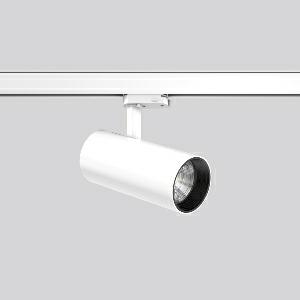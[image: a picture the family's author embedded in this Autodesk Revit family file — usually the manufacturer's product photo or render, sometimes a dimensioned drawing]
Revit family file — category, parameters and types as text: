
# Revit family: deecos_s_mini_742200_002_2_e126
name_source: partatom
category: Lighting Fixtures
units: mm (PartAtom-declared; Revit-internal decimal feet)

## family parameters
Cut with Voids When Loaded = No
Host = Face
Light Source = No
Part Type = Normal
Room Calculation Point = No
Round Connector Dimension = Use Diameter
Shared = No

## types (1)
- DEECOS S mini (1 x LED Modul 927, 1900 lm, 2700)
    Apparent Load = 20 VA
    Approval mark = CE
    CIE Flux Codes = 98 100 100 100 100
    Color Rendering = 92
    Color Temperature = 2700
    Default Elevation = 1800 mm
    Description = Series: DEECOS S mini
LED surface-mounted projector in modern design with no visible cooling ribs. Housing: die-cast aluminium, powder-coated. Rotation range: 356°. Swivel range: 90°. Black plastic ring and recessed LED to prevent glare from the side. Optical assembly with lens made of plastic (polycarbonate) for the best homogeneous light distribution - can be changed without tools. Best colour rendering index Ra>90. With multi adaptor for 3-circuit tracks 230 V. Suitable for Track on ceiling, Wall track. High quality converter without flickering and stroboscopic effect. The following accessories can be mounted without use of tools: interchangeable lenses, decorative glasses, honeycomb louvre, clear and frosted diffusers, white interchangeable plastic ring. 
Colour: traffic white, matt (RAL 9016)
Diameter: 87 mm
Height: 214 mm
Lamp: LED
Socket: without socket
Colour temperature: 2700K
Colour rendering index (CRI): 92
System power: 20 W
Rated luminous flux: 1900 lm
Luminous efficiency: 95 lm/W
Control gear: Regulated power supply
Protection class: I
Type of protection: IP 20
    Height = 214 mm
    Lamp = 1 x LED Modul 927
    Lamp Light Flux = 1900 lm
    Lamp count = 1
    Length = 87 mm
    Lifetime = 50000 h
    Luminous efficacy = 95 lm/W
    Manufacturer = RZB
    ModVariant = No
    Model = 742200.002.2
    Mounting Place = Ceiling
    Mounting Type = Rail mounted
    Number of Poles = 1
    OnlyDefault = Yes
    Power Factor = 1
    Product Name = DEECOS S mini
    Product group = Track mounted projectors
    ProductGroupID = 301
    Protection Class = Protection class I
    Protection Degree = IP 20
    RLX_Detail_Level = 1
    RLX_Emergency_Light_Flux = 0 lm
    RLX_Emergency_Type = 0
    RLX_Emergency_Type_DB = No
    RlxData = <blob elided: 35301 chars, md5=cb18b95b>
    Socket = socket
    Standby Power = 0 W
    System Light Flux = 1900 lm
    System Power = 20 W
    Type Comments = Product without accessories
    Type Image = 741930.002.jpg
    URL = http://relux.com
    VarID = ---
    Voltage = 230 V
    Voltage Range = 220-240 V
    Weight = 0.00 kg
    Width = 0 mm  [stored 0 ft]

note: [stored X ft] marks values corroborated as IEEE doubles in the binary element streams (Revit-internal decimal feet)

## geometry (parser evidence)
native form markers: Blend x4, Sweep x11
no freeform markers — native parametric forms only
